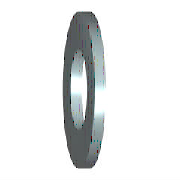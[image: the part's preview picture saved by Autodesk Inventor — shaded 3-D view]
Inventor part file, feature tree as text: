
AUTODESK INVENTOR PART (.ipt)
format: ipt  version: 2022 (Build 260153000, 153)  size: 108,032 bytes
history: native  units: mm (DEFAULTED — no unit token found)
features: other x1, plane x1, sketch x1
ambient origin geometry x7: Origin, YZ Plane, XY Plane, X Axis, Y Axis, Z Axis, Center Point
bodies: Solid1 (feature_tree), Body (feature_tree)
feature tree (3):
  other  "Work Axis1"
  plane  "Work Plane1"
  sketch  "Sketch"  dims[d0=8.4mm d1=16.0mm d2=1.6mm d3=0.0mm d4=0.0mm d5=0.0mm d6=0.0mm d7=0.0mm]
